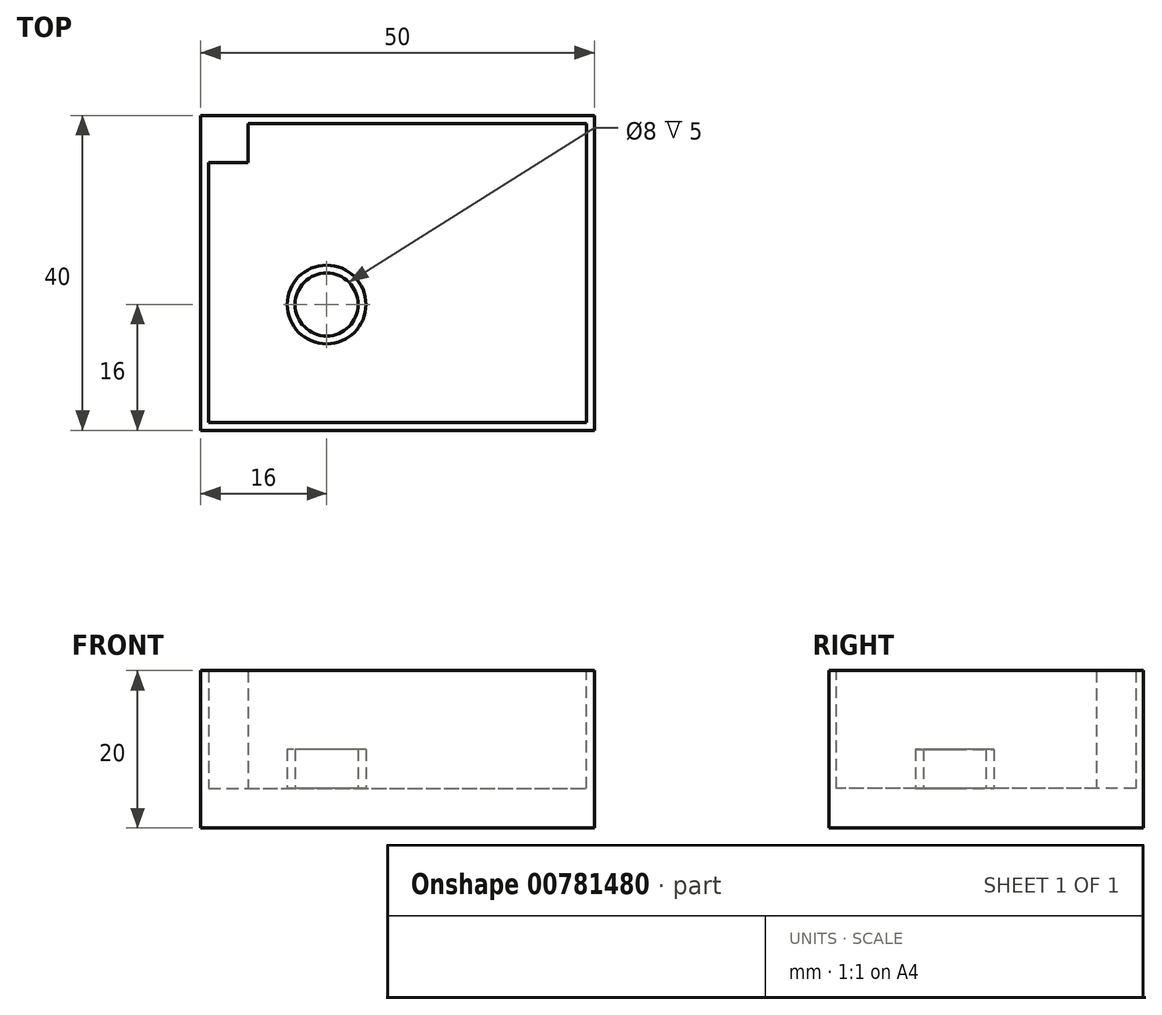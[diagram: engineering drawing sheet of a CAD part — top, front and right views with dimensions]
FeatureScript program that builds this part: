
annotation { "Feature Type Name" : "Feature", "Feature Type Description" : "" }
export const myFeature = defineFeature(function(context is Context, id is Id, definition is map)
    precondition{}
    {
        {
            var Q0;
            Q0=qCreatedBy(makeId("Top.planeOp"),FACE);
            var sketch = newSketch(context, id + "F0", { "sketchPlane" : qUnion([Q0])});
            skLineSegment(sketch, "E0.bottom", {"start": v(-25, 20) * mm, "end": v(25, 20) * mm});
            skLineSegment(sketch, "E0.top", {"start": v(-25, -20) * mm, "end": v(25, -20) * mm});
            skLineSegment(sketch, "E0.left", {"start": v(-25, 20) * mm, "end": v(-25, -20) * mm});
            skLineSegment(sketch, "E0.right", {"start": v(25, 20) * mm, "end": v(25, -20) * mm});
            skPoint(sketch, "E0.middle", {"position": v(0, 0) * mm});
            skSolve(sketch);
        }
        {
            var Q0;
            Q0=makeQuery(id+"F0.imprint","IMPRINT",FACE,{"disambiguationData":[TD([[makeQuery(id+"F0.imprint","IMPRINT",EDGE,{"derivedFrom":sQuery(id+"F0.wireOp",EDGE,"E0.bottom")}),-1.0]])]});
            extrude(context, id + "F1", {"entities" : qUnion([Q0]), "depth" : 20 * mm, "offsetDistance" : 25 * mm});
        }
        {
            var Q0;
            Q0=makeQuery(id+"F1.opExtrude","CAP_FACE",FACE,{"disambiguationData":[OSD([sQuery(id+"F0.wireOp",EDGE,"E0.bottom"),sQuery(id+"F0.wireOp",EDGE,"E0.top"),sQuery(id+"F0.wireOp",EDGE,"E0.left"),sQuery(id+"F0.wireOp",EDGE,"E0.right")])],"isStart":false});
            var sketch = newSketch(context, id + "F2", { "sketchPlane" : qUnion([Q0])});
            skLineSegment(sketch, "E1.bottom", {"start": v(-24, 19) * mm, "end": v(24, 19) * mm});
            skLineSegment(sketch, "E1.top", {"start": v(-24, -19) * mm, "end": v(24, -19) * mm});
            skLineSegment(sketch, "E1.left", {"start": v(-24, 19) * mm, "end": v(-24, -19) * mm});
            skLineSegment(sketch, "E1.right", {"start": v(24, 19) * mm, "end": v(24, -19) * mm});
            skPoint(sketch, "E1.middle", {"position": v(0, 0) * mm});
            skSolve(sketch);
        }
        {
            var Q0;
            Q0 = qSketchRegion(id + "F2", true);
            extrude(context, id + "F3", {"entities" : qUnion([Q0]), "operationType" : NewBodyOperationType.REMOVE, "oppositeDirection" : true, "depth" : 15 * mm, "offsetDistance" : 25 * mm});
        }
        {
            var Q0;
            Q0=makeQuery(id+"F3.boolean.opBoolean","COPY",FACE,{"derivedFrom":makeQuery(id+"F3.opExtrude","CAP_FACE",FACE,{"disambiguationData":[OSD([sQuery(id+"F2.wireOp",EDGE,"E1.bottom"),sQuery(id+"F2.wireOp",EDGE,"E1.top"),sQuery(id+"F2.wireOp",EDGE,"E1.left"),sQuery(id+"F2.wireOp",EDGE,"E1.right")])],"isStart":false})});
            var sketch = newSketch(context, id + "F4", { "sketchPlane" : qUnion([Q0])});
            skLineSegment(sketch, "E2.bottom", {"start": v(-24, 19) * mm, "end": v(-19, 19) * mm});
            skLineSegment(sketch, "E2.top", {"start": v(-24, 14) * mm, "end": v(-19, 14) * mm});
            skLineSegment(sketch, "E2.left", {"start": v(-24, 19) * mm, "end": v(-24, 14) * mm});
            skLineSegment(sketch, "E2.right", {"start": v(-19, 19) * mm, "end": v(-19, 14) * mm});
            skSolve(sketch);
        }
        {
            var Q0;
            Q0 = qSketchRegion(id + "F4", true);
            extrude(context, id + "F5", {"entities" : qUnion([Q0]), "operationType" : NewBodyOperationType.ADD, "depth" : 15 * mm, "offsetDistance" : 25 * mm});
        }
        {
            var Q0;
            Q0=makeQuery(id+"F3.boolean.opBoolean","COPY",FACE,{"derivedFrom":makeQuery(id+"F3.opExtrude","CAP_FACE",FACE,{"disambiguationData":[OSD([sQuery(id+"F2.wireOp",EDGE,"E1.bottom"),sQuery(id+"F2.wireOp",EDGE,"E1.top"),sQuery(id+"F2.wireOp",EDGE,"E1.left"),sQuery(id+"F2.wireOp",EDGE,"E1.right")])],"isStart":false})});
            var sketch = newSketch(context, id + "F6", { "sketchPlane" : qUnion([Q0])});
            skCircle(sketch, "E3", {"center": v(-9, -4) * mm, "radius": 5 * mm});
            skCircle(sketch, "E4", {"center": v(-9, -4) * mm, "radius": 4 * mm});
            skSolve(sketch);
        }
        {
            var Q0;
            Q0=makeQuery(id+"F6.imprint","IMPRINT",FACE,{"disambiguationData":[TD([[makeQuery(id+"F6.imprint","IMPRINT",EDGE,{"derivedFrom":sQuery(id+"F6.wireOp",EDGE,"E3")}),1.0]])]});
            extrude(context, id + "F7", {"entities" : qUnion([Q0]), "operationType" : NewBodyOperationType.ADD, "depth" : 5 * mm, "offsetDistance" : 25 * mm});
        }
    });
